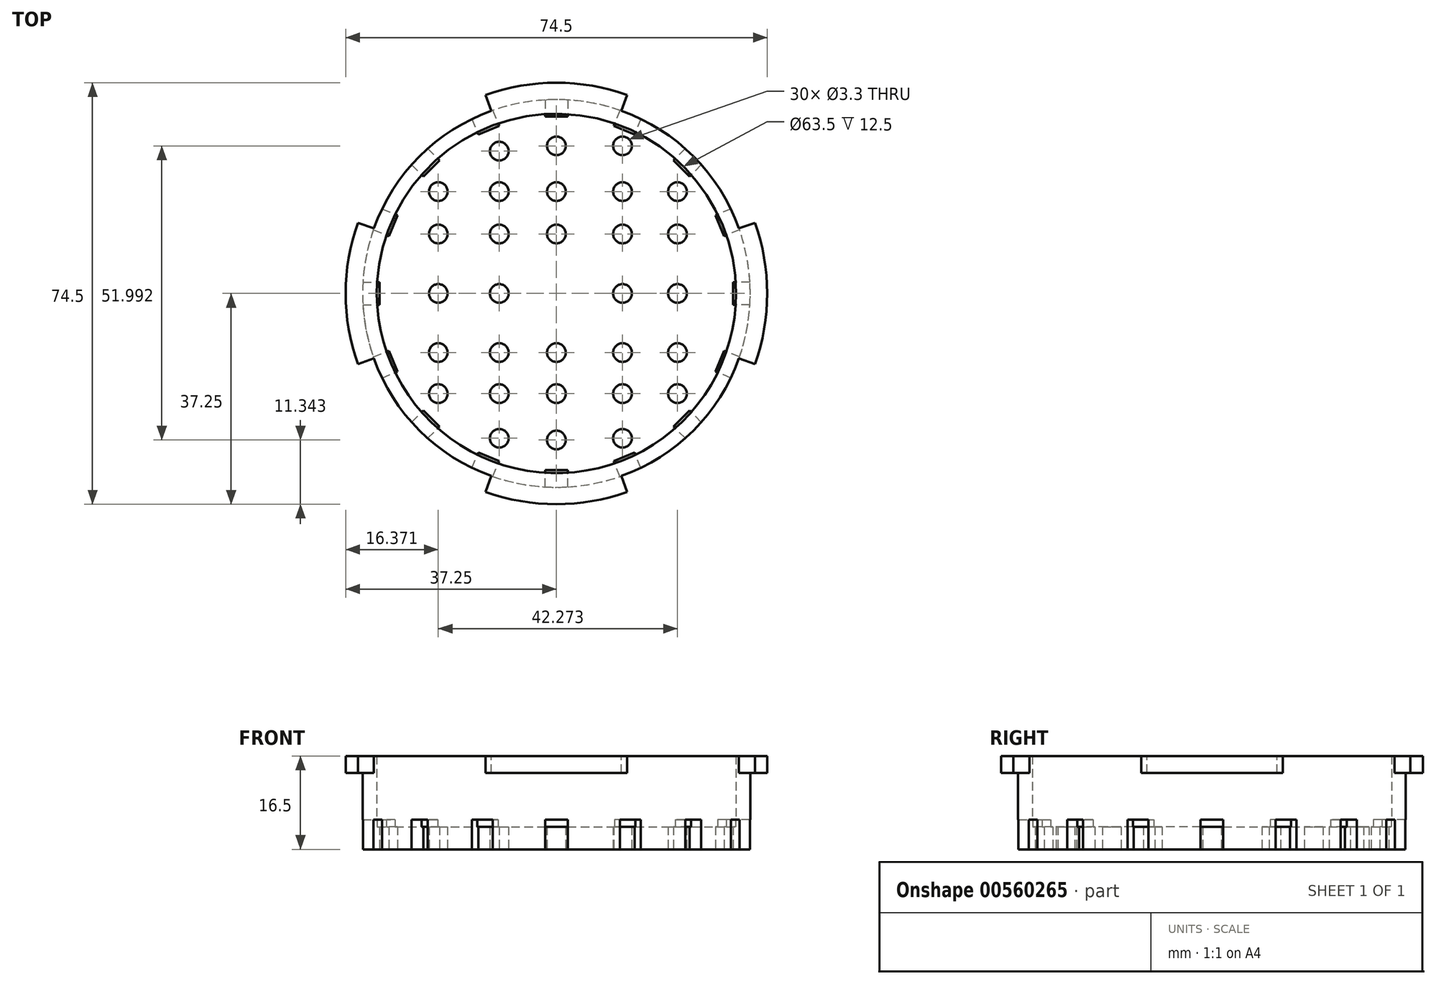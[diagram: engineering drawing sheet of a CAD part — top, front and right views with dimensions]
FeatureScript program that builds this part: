
annotation { "Feature Type Name" : "Feature", "Feature Type Description" : "" }
export const myFeature = defineFeature(function(context is Context, id is Id, definition is map)
    precondition{}
    {
        {
            var Q0;
            Q0=qCreatedBy(makeId("Top.planeOp"),FACE);
            var sketch = newSketch(context, id + "F0", { "sketchPlane" : qUnion([Q0])});
            skCircle(sketch, "E0", {"center": v(0, 0) * mm, "radius": 34.25 * mm});
            skCircle(sketch, "E1", {"center": v(0, 0) * mm, "radius": 31.75 * mm});
            skSolve(sketch);
        }
        {
            var Q0;
            Q0=makeQuery(id+"F0.imprint","IMPRINT",FACE,{"disambiguationData":[TD([[makeQuery(id+"F0.imprint","IMPRINT",EDGE,{"derivedFrom":sQuery(id+"F0.wireOp",EDGE,"E0")}),1.0]])]});
            extrude(context, id + "F1", {"entities" : qUnion([Q0]), "depth" : 16.5 * mm, "offsetDistance" : 25 * mm});
        }
        {
            var Q0;
            Q0=makeQuery(id+"F1.opExtrude","CAP_FACE",FACE,{"disambiguationData":[OSD([sQuery(id+"F0.wireOp",EDGE,"E0"),sQuery(id+"F0.wireOp",EDGE,"E1")])],"isStart":true});
            var sketch = newSketch(context, id + "F2", { "sketchPlane" : qUnion([Q0])});
            skCircle(sketch, "E2.0", {"center": v(0, 0) * mm, "radius": 31.75 * mm});
            skSolve(sketch);
        }
        {
            var Q0;
            Q0=makeQuery(id+"F2.imprint","IMPRINT",FACE,{"disambiguationData":[TD([[makeQuery(id+"F2.imprint","IMPRINT",EDGE,{"derivedFrom":sQuery(id+"F2.wireOp",EDGE,"E2.0")}),-1.0]])]});
            extrude(context, id + "F3", {"entities" : qUnion([Q0]), "operationType" : NewBodyOperationType.ADD, "oppositeDirection" : true, "depth" : 4 * mm, "offsetDistance" : 25 * mm});
        }
        {
            var Q0;
            Q0=makeQuery(id+"F3.boolean.opBoolean","MERGE",FACE,{"derivedFrom":[makeQuery(id+"F1.opExtrude","CAP_FACE",FACE,{"disambiguationData":[OSD([sQuery(id+"F0.wireOp",EDGE,"E0"),sQuery(id+"F0.wireOp",EDGE,"E1")])],"isStart":true}),makeQuery(id+"F3.opExtrude","CAP_FACE",FACE,{"disambiguationData":[OSD([sQuery(id+"F2.wireOp",EDGE,"E2.0")])],"isStart":true})]});
            var sketch = newSketch(context, id + "F4", { "sketchPlane" : qUnion([Q0])});
            skLineSegment(sketch, "E3.bottom", {"start": v(-2, 37.25) * mm, "end": v(2, 37.25) * mm});
            skLineSegment(sketch, "E3.top", {"start": v(-2, 31.25) * mm, "end": v(2, 31.25) * mm});
            skLineSegment(sketch, "E3.left", {"start": v(-2, 37.25) * mm, "end": v(-2, 31.25) * mm});
            skLineSegment(sketch, "E3.right", {"start": v(2, 37.25) * mm, "end": v(2, 31.25) * mm});
            skPoint(sketch, "E3.middle", {"position": v(0, 34.25) * mm});
            skLineSegment(sketch, "E4.1.0", {"start": v(-12.4, 35.18) * mm, "end": v(-10.11, 29.64) * mm});
            skLineSegment(sketch, "E4.1.1", {"start": v(-16.1, 33.65) * mm, "end": v(-13.8, 28.1) * mm});
            skLineSegment(sketch, "E4.1.2", {"start": v(-13.8, 28.1) * mm, "end": v(-10.11, 29.64) * mm});
            skLineSegment(sketch, "E4.1.3", {"start": v(-16.1, 33.65) * mm, "end": v(-12.4, 35.18) * mm});
            skPoint(sketch, "E4.1.4", {"position": v(-13.1, 31.64) * mm});
            skLineSegment(sketch, "E4.2.0", {"start": v(-24.93, 27.75) * mm, "end": v(-20.68, 23.51) * mm});
            skLineSegment(sketch, "E4.2.1", {"start": v(-27.75, 24.93) * mm, "end": v(-23.51, 20.68) * mm});
            skLineSegment(sketch, "E4.2.2", {"start": v(-23.51, 20.68) * mm, "end": v(-20.68, 23.51) * mm});
            skLineSegment(sketch, "E4.2.3", {"start": v(-27.75, 24.93) * mm, "end": v(-24.93, 27.75) * mm});
            skPoint(sketch, "E4.2.4", {"position": v(-24.22, 24.22) * mm});
            skLineSegment(sketch, "E4.3.0", {"start": v(-33.65, 16.1) * mm, "end": v(-28.1, 13.8) * mm});
            skLineSegment(sketch, "E4.3.1", {"start": v(-35.18, 12.4) * mm, "end": v(-29.64, 10.11) * mm});
            skLineSegment(sketch, "E4.3.2", {"start": v(-29.64, 10.11) * mm, "end": v(-28.1, 13.8) * mm});
            skLineSegment(sketch, "E4.3.3", {"start": v(-35.18, 12.4) * mm, "end": v(-33.65, 16.1) * mm});
            skPoint(sketch, "E4.3.4", {"position": v(-31.64, 13.1) * mm});
            skLineSegment(sketch, "E4.4.0", {"start": v(-37.25, 2) * mm, "end": v(-31.25, 2) * mm});
            skLineSegment(sketch, "E4.4.1", {"start": v(-37.25, -2) * mm, "end": v(-31.25, -2) * mm});
            skLineSegment(sketch, "E4.4.2", {"start": v(-31.25, -2) * mm, "end": v(-31.25, 2) * mm});
            skLineSegment(sketch, "E4.4.3", {"start": v(-37.25, -2) * mm, "end": v(-37.25, 2) * mm});
            skPoint(sketch, "E4.4.4", {"position": v(-34.25, 0) * mm});
            skLineSegment(sketch, "E4.5.0", {"start": v(-35.18, -12.4) * mm, "end": v(-29.64, -10.11) * mm});
            skLineSegment(sketch, "E4.5.1", {"start": v(-33.65, -16.1) * mm, "end": v(-28.1, -13.8) * mm});
            skLineSegment(sketch, "E4.5.2", {"start": v(-28.1, -13.8) * mm, "end": v(-29.64, -10.11) * mm});
            skLineSegment(sketch, "E4.5.3", {"start": v(-33.65, -16.1) * mm, "end": v(-35.18, -12.4) * mm});
            skPoint(sketch, "E4.5.4", {"position": v(-31.64, -13.1) * mm});
            skLineSegment(sketch, "E4.6.0", {"start": v(-27.75, -24.93) * mm, "end": v(-23.51, -20.68) * mm});
            skLineSegment(sketch, "E4.6.1", {"start": v(-24.93, -27.75) * mm, "end": v(-20.68, -23.51) * mm});
            skLineSegment(sketch, "E4.6.2", {"start": v(-20.68, -23.51) * mm, "end": v(-23.51, -20.68) * mm});
            skLineSegment(sketch, "E4.6.3", {"start": v(-24.93, -27.75) * mm, "end": v(-27.75, -24.93) * mm});
            skPoint(sketch, "E4.6.4", {"position": v(-24.22, -24.22) * mm});
            skLineSegment(sketch, "E4.7.0", {"start": v(-16.1, -33.65) * mm, "end": v(-13.8, -28.1) * mm});
            skLineSegment(sketch, "E4.7.1", {"start": v(-12.4, -35.18) * mm, "end": v(-10.11, -29.64) * mm});
            skLineSegment(sketch, "E4.7.2", {"start": v(-10.11, -29.64) * mm, "end": v(-13.8, -28.1) * mm});
            skLineSegment(sketch, "E4.7.3", {"start": v(-12.4, -35.18) * mm, "end": v(-16.1, -33.65) * mm});
            skPoint(sketch, "E4.7.4", {"position": v(-13.1, -31.64) * mm});
            skLineSegment(sketch, "E4.8.0", {"start": v(-2, -37.25) * mm, "end": v(-2, -31.25) * mm});
            skLineSegment(sketch, "E4.8.1", {"start": v(2, -37.25) * mm, "end": v(2, -31.25) * mm});
            skLineSegment(sketch, "E4.8.2", {"start": v(2, -31.25) * mm, "end": v(-2, -31.25) * mm});
            skLineSegment(sketch, "E4.8.3", {"start": v(2, -37.25) * mm, "end": v(-2, -37.25) * mm});
            skPoint(sketch, "E4.8.4", {"position": v(0, -34.25) * mm});
            skLineSegment(sketch, "E4.9.0", {"start": v(12.4, -35.18) * mm, "end": v(10.11, -29.64) * mm});
            skLineSegment(sketch, "E4.9.1", {"start": v(16.1, -33.65) * mm, "end": v(13.8, -28.1) * mm});
            skLineSegment(sketch, "E4.9.2", {"start": v(13.8, -28.1) * mm, "end": v(10.11, -29.64) * mm});
            skLineSegment(sketch, "E4.9.3", {"start": v(16.1, -33.65) * mm, "end": v(12.4, -35.18) * mm});
            skPoint(sketch, "E4.9.4", {"position": v(13.1, -31.64) * mm});
            skLineSegment(sketch, "E4.10.0", {"start": v(24.93, -27.75) * mm, "end": v(20.68, -23.51) * mm});
            skLineSegment(sketch, "E4.10.1", {"start": v(27.75, -24.93) * mm, "end": v(23.51, -20.68) * mm});
            skLineSegment(sketch, "E4.10.2", {"start": v(23.51, -20.68) * mm, "end": v(20.68, -23.51) * mm});
            skLineSegment(sketch, "E4.10.3", {"start": v(27.75, -24.93) * mm, "end": v(24.93, -27.75) * mm});
            skPoint(sketch, "E4.10.4", {"position": v(24.22, -24.22) * mm});
            skLineSegment(sketch, "E4.11.0", {"start": v(33.65, -16.1) * mm, "end": v(28.1, -13.8) * mm});
            skLineSegment(sketch, "E4.11.1", {"start": v(35.18, -12.4) * mm, "end": v(29.64, -10.11) * mm});
            skLineSegment(sketch, "E4.11.2", {"start": v(29.64, -10.11) * mm, "end": v(28.1, -13.8) * mm});
            skLineSegment(sketch, "E4.11.3", {"start": v(35.18, -12.4) * mm, "end": v(33.65, -16.1) * mm});
            skPoint(sketch, "E4.11.4", {"position": v(31.64, -13.1) * mm});
            skLineSegment(sketch, "E4.12.0", {"start": v(37.25, -2) * mm, "end": v(31.25, -2) * mm});
            skLineSegment(sketch, "E4.12.1", {"start": v(37.25, 2) * mm, "end": v(31.25, 2) * mm});
            skLineSegment(sketch, "E4.12.2", {"start": v(31.25, 2) * mm, "end": v(31.25, -2) * mm});
            skLineSegment(sketch, "E4.12.3", {"start": v(37.25, 2) * mm, "end": v(37.25, -2) * mm});
            skPoint(sketch, "E4.12.4", {"position": v(34.25, 0) * mm});
            skLineSegment(sketch, "E4.13.0", {"start": v(35.18, 12.4) * mm, "end": v(29.64, 10.11) * mm});
            skLineSegment(sketch, "E4.13.1", {"start": v(33.65, 16.1) * mm, "end": v(28.1, 13.8) * mm});
            skLineSegment(sketch, "E4.13.2", {"start": v(28.1, 13.8) * mm, "end": v(29.64, 10.11) * mm});
            skLineSegment(sketch, "E4.13.3", {"start": v(33.65, 16.1) * mm, "end": v(35.18, 12.4) * mm});
            skPoint(sketch, "E4.13.4", {"position": v(31.64, 13.1) * mm});
            skLineSegment(sketch, "E4.14.0", {"start": v(27.75, 24.93) * mm, "end": v(23.51, 20.68) * mm});
            skLineSegment(sketch, "E4.14.1", {"start": v(24.93, 27.75) * mm, "end": v(20.68, 23.51) * mm});
            skLineSegment(sketch, "E4.14.2", {"start": v(20.68, 23.51) * mm, "end": v(23.51, 20.68) * mm});
            skLineSegment(sketch, "E4.14.3", {"start": v(24.93, 27.75) * mm, "end": v(27.75, 24.93) * mm});
            skPoint(sketch, "E4.14.4", {"position": v(24.22, 24.22) * mm});
            skLineSegment(sketch, "E4.15.0", {"start": v(16.1, 33.65) * mm, "end": v(13.8, 28.1) * mm});
            skLineSegment(sketch, "E4.15.1", {"start": v(12.4, 35.18) * mm, "end": v(10.11, 29.64) * mm});
            skLineSegment(sketch, "E4.15.2", {"start": v(10.11, 29.64) * mm, "end": v(13.8, 28.1) * mm});
            skLineSegment(sketch, "E4.15.3", {"start": v(12.4, 35.18) * mm, "end": v(16.1, 33.65) * mm});
            skPoint(sketch, "E4.15.4", {"position": v(13.1, 31.64) * mm});
            skPoint(sketch, "E4.center", {"position": v(0, 0) * mm});
            skSolve(sketch);
        }
        {
            var Q0;
            {var subQ0=sQuery(id+"F4.wireOp",EDGE,"E4.14.2");Q0=makeQuery(id+"F4.imprint","IMPRINT",FACE,{"disambiguationData":[TD([[makeQuery(id+"F4.imprint","IMPRINT",EDGE,{"derivedFrom":subQ0}),1.0]])]});}
            var Q1;
            {var subQ0=sQuery(id+"F4.wireOp",EDGE,"E4.15.2");Q1=makeQuery(id+"F4.imprint","IMPRINT",FACE,{"disambiguationData":[TD([[makeQuery(id+"F4.imprint","IMPRINT",EDGE,{"derivedFrom":subQ0}),1.0]])]});}
            var Q2;
            {var subQ0=sQuery(id+"F4.wireOp",EDGE,"E3.top");Q2=makeQuery(id+"F4.imprint","IMPRINT",FACE,{"disambiguationData":[TD([[makeQuery(id+"F4.imprint","IMPRINT",EDGE,{"derivedFrom":subQ0}),1.0]])]});}
            var Q3;
            {var subQ0=sQuery(id+"F4.wireOp",EDGE,"E4.1.2");Q3=makeQuery(id+"F4.imprint","IMPRINT",FACE,{"disambiguationData":[TD([[makeQuery(id+"F4.imprint","IMPRINT",EDGE,{"derivedFrom":subQ0}),1.0]])]});}
            var Q4;
            {var subQ0=sQuery(id+"F4.wireOp",EDGE,"E4.2.2");Q4=makeQuery(id+"F4.imprint","IMPRINT",FACE,{"disambiguationData":[TD([[makeQuery(id+"F4.imprint","IMPRINT",EDGE,{"derivedFrom":subQ0}),1.0]])]});}
            var Q5;
            {var subQ0=sQuery(id+"F4.wireOp",EDGE,"E4.4.2");Q5=makeQuery(id+"F4.imprint","IMPRINT",FACE,{"disambiguationData":[TD([[makeQuery(id+"F4.imprint","IMPRINT",EDGE,{"derivedFrom":subQ0}),1.0]])]});}
            var Q6;
            {var subQ0=sQuery(id+"F4.wireOp",EDGE,"E4.5.2");Q6=makeQuery(id+"F4.imprint","IMPRINT",FACE,{"disambiguationData":[TD([[makeQuery(id+"F4.imprint","IMPRINT",EDGE,{"derivedFrom":subQ0}),1.0]])]});}
            var Q7;
            {var subQ0=sQuery(id+"F4.wireOp",EDGE,"E4.6.2");Q7=makeQuery(id+"F4.imprint","IMPRINT",FACE,{"disambiguationData":[TD([[makeQuery(id+"F4.imprint","IMPRINT",EDGE,{"derivedFrom":subQ0}),1.0]])]});}
            var Q8;
            {var subQ0=sQuery(id+"F4.wireOp",EDGE,"E4.7.2");Q8=makeQuery(id+"F4.imprint","IMPRINT",FACE,{"disambiguationData":[TD([[makeQuery(id+"F4.imprint","IMPRINT",EDGE,{"derivedFrom":subQ0}),1.0]])]});}
            var Q9;
            {var subQ0=sQuery(id+"F4.wireOp",EDGE,"E4.8.2");Q9=makeQuery(id+"F4.imprint","IMPRINT",FACE,{"disambiguationData":[TD([[makeQuery(id+"F4.imprint","IMPRINT",EDGE,{"derivedFrom":subQ0}),1.0]])]});}
            var Q10;
            {var subQ0=sQuery(id+"F4.wireOp",EDGE,"E4.9.2");Q10=makeQuery(id+"F4.imprint","IMPRINT",FACE,{"disambiguationData":[TD([[makeQuery(id+"F4.imprint","IMPRINT",EDGE,{"derivedFrom":subQ0}),1.0]])]});}
            var Q11;
            {var subQ0=sQuery(id+"F4.wireOp",EDGE,"E4.11.2");Q11=makeQuery(id+"F4.imprint","IMPRINT",FACE,{"disambiguationData":[TD([[makeQuery(id+"F4.imprint","IMPRINT",EDGE,{"derivedFrom":subQ0}),1.0]])]});}
            var Q12;
            {var subQ0=sQuery(id+"F4.wireOp",EDGE,"E4.10.2");Q12=makeQuery(id+"F4.imprint","IMPRINT",FACE,{"disambiguationData":[TD([[makeQuery(id+"F4.imprint","IMPRINT",EDGE,{"derivedFrom":subQ0}),1.0]])]});}
            var Q13;
            {var subQ0=sQuery(id+"F4.wireOp",EDGE,"E4.12.2");Q13=makeQuery(id+"F4.imprint","IMPRINT",FACE,{"disambiguationData":[TD([[makeQuery(id+"F4.imprint","IMPRINT",EDGE,{"derivedFrom":subQ0}),1.0]])]});}
            var Q14;
            {var subQ0=sQuery(id+"F4.wireOp",EDGE,"E4.13.2");Q14=makeQuery(id+"F4.imprint","IMPRINT",FACE,{"disambiguationData":[TD([[makeQuery(id+"F4.imprint","IMPRINT",EDGE,{"derivedFrom":subQ0}),1.0]])]});}
            var Q15;
            {var subQ0=sQuery(id+"F4.wireOp",EDGE,"E4.3.2");Q15=makeQuery(id+"F4.imprint","IMPRINT",FACE,{"disambiguationData":[TD([[makeQuery(id+"F4.imprint","IMPRINT",EDGE,{"derivedFrom":subQ0}),1.0]])]});}
            extrude(context, id + "F5", {"entities" : qUnion([Q0, Q1, Q2, Q3, Q4, Q5, Q6, Q7, Q8, Q9, Q10, Q11, Q12, Q13, Q14, Q15]), "operationType" : NewBodyOperationType.REMOVE, "oppositeDirection" : true, "depth" : 5.25 * mm, "offsetDistance" : 25 * mm});
        }
        {
            var Q0;
            Q0=makeQuery(id+"F3.boolean.opBoolean","MERGE",FACE,{"derivedFrom":[makeQuery(id+"F1.opExtrude","CAP_FACE",FACE,{"disambiguationData":[OSD([sQuery(id+"F0.wireOp",EDGE,"E0"),sQuery(id+"F0.wireOp",EDGE,"E1")])],"isStart":true}),makeQuery(id+"F3.opExtrude","CAP_FACE",FACE,{"disambiguationData":[OSD([sQuery(id+"F2.wireOp",EDGE,"E2.0")])],"isStart":true})]});
            var sketch = newSketch(context, id + "F6", { "sketchPlane" : qUnion([Q0])});
            skPoint(sketch, "E5", {"position": v(0, 25.9) * mm});
            skPoint(sketch, "E6", {"position": v(0, 17.7) * mm});
            skPoint(sketch, "E7", {"position": v(0, 10.45) * mm});
            skPoint(sketch, "E8", {"position": v(0, -10.51) * mm});
            skPoint(sketch, "E9", {"position": v(0, -18) * mm});
            skPoint(sketch, "E10", {"position": v(0, -26.09) * mm});
            skPoint(sketch, "E11", {"position": v(11.67, -18) * mm});
            skPoint(sketch, "E12", {"position": v(11.67, -10.51) * mm});
            skPoint(sketch, "E13", {"position": v(11.67, 0) * mm});
            skPoint(sketch, "E14", {"position": v(11.67, 10.45) * mm});
            skPoint(sketch, "E15", {"position": v(11.67, 17.7) * mm});
            skPoint(sketch, "E16", {"position": v(11.67, 25.6) * mm});
            skPoint(sketch, "E17", {"position": v(21.4, 17.7) * mm});
            skPoint(sketch, "E18", {"position": v(21.4, 10.45) * mm});
            skPoint(sketch, "E19", {"position": v(21.4, 0) * mm});
            skPoint(sketch, "E20", {"position": v(21.4, -10.51) * mm});
            skPoint(sketch, "E21", {"position": v(21.4, -18) * mm});
            skPoint(sketch, "E22", {"position": v(11.67, -26.09) * mm});
            skPoint(sketch, "E23", {"position": v(-10.11, -25.15) * mm});
            skPoint(sketch, "E24", {"position": v(-10.11, -18) * mm});
            skPoint(sketch, "E25", {"position": v(-10.11, -10.51) * mm});
            skPoint(sketch, "E26", {"position": v(-10.11, 0) * mm});
            skPoint(sketch, "E27", {"position": v(-10.11, 10.45) * mm});
            skPoint(sketch, "E28", {"position": v(-10.11, 17.7) * mm});
            skPoint(sketch, "E29", {"position": v(-10.11, 25.6) * mm});
            skPoint(sketch, "E30", {"position": v(-20.88, 0) * mm});
            skPoint(sketch, "E31", {"position": v(-20.88, 10.45) * mm});
            skPoint(sketch, "E32", {"position": v(-20.88, 17.7) * mm});
            skPoint(sketch, "E33", {"position": v(-20.88, -10.51) * mm});
            skPoint(sketch, "E34", {"position": v(-20.88, -18) * mm});
            skSolve(sketch);
        }
        {
            var Q0;
            Q0=sQuery(id+"F6.wireOp",VERTEX,"E26");
            var Q1;
            Q1=sQuery(id+"F6.wireOp",VERTEX,"E27");
            var Q2;
            Q2=sQuery(id+"F6.wireOp",VERTEX,"E28");
            var Q3;
            Q3=sQuery(id+"F6.wireOp",VERTEX,"E32");
            var Q4;
            Q4=sQuery(id+"F6.wireOp",VERTEX,"E31");
            var Q5;
            Q5=sQuery(id+"F6.wireOp",VERTEX,"E30");
            var Q6;
            Q6=sQuery(id+"F6.wireOp",VERTEX,"E33");
            var Q7;
            Q7=sQuery(id+"F6.wireOp",VERTEX,"E34");
            var Q8;
            Q8=sQuery(id+"F6.wireOp",VERTEX,"E23");
            var Q9;
            Q9=sQuery(id+"F6.wireOp",VERTEX,"E24");
            var Q10;
            Q10=sQuery(id+"F6.wireOp",VERTEX,"E25");
            var Q11;
            Q11=sQuery(id+"F6.wireOp",VERTEX,"E9");
            var Q12;
            Q12=sQuery(id+"F6.wireOp",VERTEX,"E8");
            var Q13;
            Q13=sQuery(id+"F6.wireOp",VERTEX,"E10");
            var Q14;
            Q14=sQuery(id+"F6.wireOp",VERTEX,"E7");
            var Q15;
            Q15=sQuery(id+"F6.wireOp",VERTEX,"E6");
            var Q16;
            Q16=sQuery(id+"F6.wireOp",VERTEX,"E29");
            var Q17;
            Q17=sQuery(id+"F6.wireOp",VERTEX,"E16");
            var Q18;
            Q18=sQuery(id+"F6.wireOp",VERTEX,"E5");
            var Q19;
            Q19=sQuery(id+"F6.wireOp",VERTEX,"E15");
            var Q20;
            Q20=sQuery(id+"F6.wireOp",VERTEX,"E14");
            var Q21;
            Q21=sQuery(id+"F6.wireOp",VERTEX,"E13");
            var Q22;
            Q22=sQuery(id+"F6.wireOp",VERTEX,"E12");
            var Q23;
            Q23=sQuery(id+"F6.wireOp",VERTEX,"E22");
            var Q24;
            Q24=sQuery(id+"F6.wireOp",VERTEX,"E21");
            var Q25;
            Q25=sQuery(id+"F6.wireOp",VERTEX,"E11");
            var Q26;
            Q26=sQuery(id+"F6.wireOp",VERTEX,"E20");
            var Q27;
            Q27=sQuery(id+"F6.wireOp",VERTEX,"E19");
            var Q28;
            Q28=sQuery(id+"F6.wireOp",VERTEX,"E18");
            var Q29;
            Q29=sQuery(id+"F6.wireOp",VERTEX,"E17");
            var Q30;
            Q30=makeQuery(id+"F1.opExtrude","SWEPT_BODY",BODY,{"disambiguationData":[OSD([sQuery(id+"F0.wireOp",EDGE,"E0"),sQuery(id+"F0.wireOp",EDGE,"E1")])]});
            hole(context, id + "F7", {"style" : HoleStyle.SIMPLE, "endStyle" : HoleEndStyle.THROUGH, "standardTappedOrClearance" : lookupTablePath({ "standard" : "ISO", "fit" : "Normal", "size" : "M3", "type" : "Clearance" }), "standardBlindInLast" : lookupTablePath({ "fit" : "Standard", "standard" : "ISO", "size" : "M3", "type" : "Clearance" }), "holeDiameter" : 3.3 * mm, "isTappedThrough" : true, "tappedDepth" : 12 * mm, "tapClearance" : 3, "locations" : qUnion([Q0, Q1, Q2, Q3, Q4, Q5, Q6, Q7, Q8, Q9, Q10, Q11, Q12, Q13, Q14, Q15, Q16, Q17, Q18, Q19, Q20, Q21, Q22, Q23, Q24, Q25, Q26, Q27, Q28, Q29]), "scope" : qUnion([Q30])});
        }
        {
            var Q0;
            Q0=makeQuery(id+"F1.opExtrude","CAP_FACE",FACE,{"disambiguationData":[OSD([sQuery(id+"F0.wireOp",EDGE,"E0"),sQuery(id+"F0.wireOp",EDGE,"E1")])],"isStart":false});
            var sketch = newSketch(context, id + "F8", { "sketchPlane" : qUnion([Q0])});
            skArc(sketch, "E35.0", {"start": v(12.5, 35.1) * mm, "mid": v(0, 37.25) * mm, "end": v(-12.5, 35.1) * mm});
            skLineSegment(sketch, "E36", {"start": v(-10.65, 29.9) * mm, "end": v(-12.5, 35.1) * mm});
            skLineSegment(sketch, "E37", {"start": v(10.65, 29.9) * mm, "end": v(12.5, 35.1) * mm});
            skArc(sketch, "E38.0", {"start": v(10.65, 29.9) * mm, "mid": v(0, 31.75) * mm, "end": v(-10.65, 29.9) * mm});
            skLineSegment(sketch, "E39.1.0", {"start": v(-29.9, -10.65) * mm, "end": v(-35.1, -12.5) * mm});
            skLineSegment(sketch, "E39.1.1", {"start": v(-29.9, 10.65) * mm, "end": v(-35.1, 12.5) * mm});
            skArc(sketch, "E39.1.2", {"start": v(-29.9, 10.65) * mm, "mid": v(-31.75, 0) * mm, "end": v(-29.9, -10.65) * mm});
            skArc(sketch, "E39.1.3", {"start": v(-35.1, 12.5) * mm, "mid": v(-37.25, 0) * mm, "end": v(-35.1, -12.5) * mm});
            skLineSegment(sketch, "E39.2.0", {"start": v(10.65, -29.9) * mm, "end": v(12.5, -35.1) * mm});
            skLineSegment(sketch, "E39.2.1", {"start": v(-10.65, -29.9) * mm, "end": v(-12.5, -35.1) * mm});
            skArc(sketch, "E39.2.2", {"start": v(-10.65, -29.9) * mm, "mid": v(0, -31.75) * mm, "end": v(10.65, -29.9) * mm});
            skArc(sketch, "E39.2.3", {"start": v(-12.5, -35.1) * mm, "mid": v(0, -37.25) * mm, "end": v(12.5, -35.1) * mm});
            skLineSegment(sketch, "E39.3.0", {"start": v(29.9, 10.65) * mm, "end": v(35.1, 12.5) * mm});
            skLineSegment(sketch, "E39.3.1", {"start": v(29.9, -10.65) * mm, "end": v(35.1, -12.5) * mm});
            skArc(sketch, "E39.3.2", {"start": v(29.9, -10.65) * mm, "mid": v(31.75, 0) * mm, "end": v(29.9, 10.65) * mm});
            skArc(sketch, "E39.3.3", {"start": v(35.1, -12.5) * mm, "mid": v(37.25, 0) * mm, "end": v(35.1, 12.5) * mm});
            skSolve(sketch);
        }
        {
            var Q0;
            {var subQ0=sQuery(id+"F8.wireOp",EDGE,"E39.1.3");Q0=makeQuery(id+"F8.imprint","IMPRINT",FACE,{"disambiguationData":[TD([[makeQuery(id+"F8.imprint","IMPRINT",EDGE,{"derivedFrom":subQ0}),1.0]])]});}
            var Q1;
            {var subQ0=sQuery(id+"F8.wireOp",EDGE,"E35.0");Q1=makeQuery(id+"F8.imprint","IMPRINT",FACE,{"disambiguationData":[TD([[makeQuery(id+"F8.imprint","IMPRINT",EDGE,{"derivedFrom":subQ0}),1.0]])]});}
            var Q2;
            {var subQ0=sQuery(id+"F8.wireOp",EDGE,"E39.3.3");Q2=makeQuery(id+"F8.imprint","IMPRINT",FACE,{"disambiguationData":[TD([[makeQuery(id+"F8.imprint","IMPRINT",EDGE,{"derivedFrom":subQ0}),1.0]])]});}
            var Q3;
            {var subQ0=sQuery(id+"F8.wireOp",EDGE,"E39.2.3");Q3=makeQuery(id+"F8.imprint","IMPRINT",FACE,{"disambiguationData":[TD([[makeQuery(id+"F8.imprint","IMPRINT",EDGE,{"derivedFrom":subQ0}),1.0]])]});}
            extrude(context, id + "F9", {"entities" : qUnion([Q0, Q1, Q2, Q3]), "operationType" : NewBodyOperationType.ADD, "oppositeDirection" : true, "depth" : 3 * mm, "offsetDistance" : 25 * mm});
        }
    });
